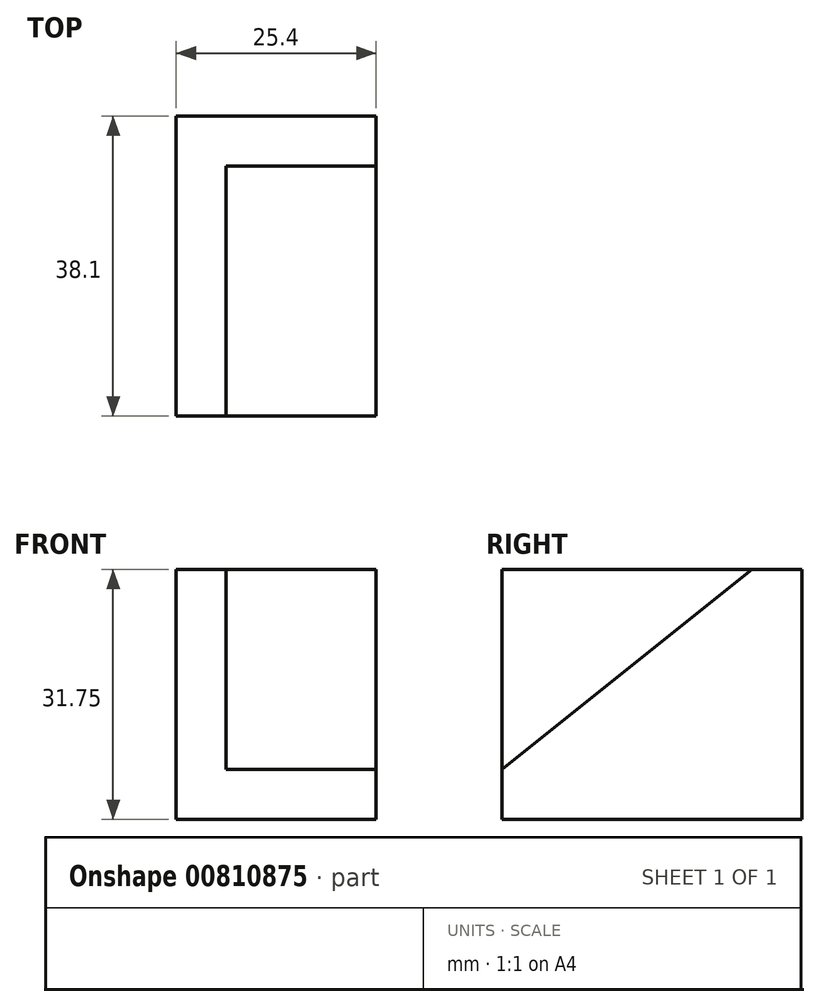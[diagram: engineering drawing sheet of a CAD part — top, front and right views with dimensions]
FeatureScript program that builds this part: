
annotation { "Feature Type Name" : "Feature", "Feature Type Description" : "" }
export const myFeature = defineFeature(function(context is Context, id is Id, definition is map)
    precondition{}
    {
        {
            var Q0;
            Q0=qCreatedBy(makeId("Right.planeOp"),FACE);
            var sketch = newSketch(context, id + "F0", { "sketchPlane" : qUnion([Q0])});
            skLineSegment(sketch, "E0.bottom", {"start": v(0, 0) * mm, "end": v(38.1, 0) * mm});
            skLineSegment(sketch, "E0.top", {"start": v(0, 31.75) * mm, "end": v(38.1, 31.75) * mm});
            skLineSegment(sketch, "E0.left", {"start": v(0, 0) * mm, "end": v(0, 31.75) * mm});
            skLineSegment(sketch, "E0.right", {"start": v(38.1, 0) * mm, "end": v(38.1, 31.75) * mm});
            skLineSegment(sketch, "E1", {"start": v(38.1, 31.75) * mm, "end": v(31.75, 31.75) * mm});
            skSolve(sketch);
        }
        {
            var Q0;
            Q0 = qSketchRegion(id + "F0", true);
            extrude(context, id + "F1", {"entities" : qUnion([Q0]), "depth" : 25.4 * mm, "offsetDistance" : 25.4 * mm});
        }
        {
            var Q0;
            Q0=makeQuery(id+"F1.opExtrude","CAP_FACE",FACE,{"disambiguationData":[OSD([sQuery(id+"F0.wireOp",EDGE,"E0.bottom"),sQuery(id+"F0.wireOp",EDGE,"E0.top"),sQuery(id+"F0.wireOp",EDGE,"E0.left"),sQuery(id+"F0.wireOp",EDGE,"E0.right"),sQuery(id+"F0.wireOp",EDGE,"E1")])],"isStart":false});
            var sketch = newSketch(context, id + "F2", { "sketchPlane" : qUnion([Q0])});
            skLineSegment(sketch, "E2", {"start": v(38.1, 31.75) * mm, "end": v(31.75, 31.75) * mm});
            skLineSegment(sketch, "E3", {"start": v(0, 0) * mm, "end": v(0, 6.35) * mm});
            skLineSegment(sketch, "E4", {"start": v(0, 6.35) * mm, "end": v(31.75, 31.75) * mm});
            skSolve(sketch);
        }
        {
            var Q0;
            Q0 = qSketchRegion(id + "F2", true);
            var Q1;
            {var subQ0=sQuery(id+"F2.wireOp",EDGE,"E4");Q1=makeQuery(id+"F2.imprint","IMPRINT",FACE,{"disambiguationData":[TD([[makeQuery(id+"F2.imprint","IMPRINT",EDGE,{"derivedFrom":subQ0}),1.0]])]});}
            extrude(context, id + "F3", {"entities" : qUnion([Q0, Q1]), "operationType" : NewBodyOperationType.REMOVE, "oppositeDirection" : true, "depth" : 19.05 * mm, "offsetDistance" : 25.4 * mm});
        }
    });
